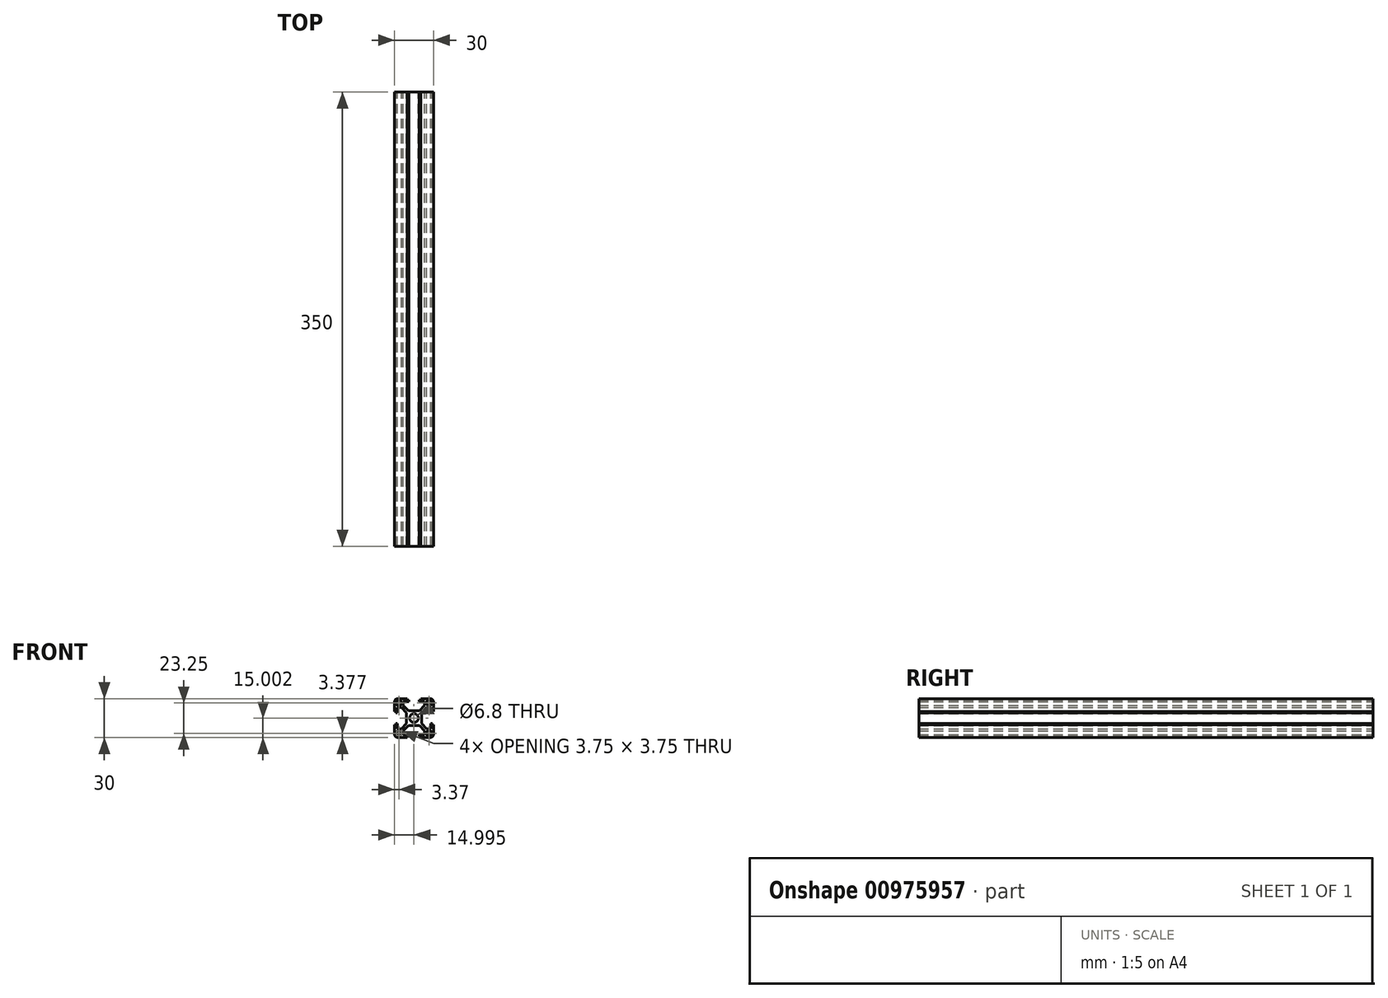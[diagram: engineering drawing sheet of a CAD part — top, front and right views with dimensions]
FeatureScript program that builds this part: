
annotation { "Feature Type Name" : "Feature", "Feature Type Description" : "" }
export const myFeature = defineFeature(function(context is Context, id is Id, definition is map)
    precondition{}
    {
        {
            var Q0;
            Q0=qCreatedBy(makeId("Front.planeOp"),FACE);
            var sketch = newSketch(context, id + "F0", { "sketchPlane" : qUnion([Q0])});
            skLineSegment(sketch, "E0.bottom", {"start": v(-60.67, 38.6) * mm, "end": v(-67.97, 38.6) * mm});
            skLineSegment(sketch, "E0.top", {"start": v(-60.67, 68.6) * mm, "end": v(-67.97, 68.6) * mm});
            skLineSegment(sketch, "E0.left", {"start": v(-58.17, 41.1) * mm, "end": v(-58.17, 48.4) * mm});
            skLineSegment(sketch, "E0.right", {"start": v(-88.17, 41.1) * mm, "end": v(-88.17, 48.4) * mm});
            skPoint(sketch, "E0.middle", {"position": v(-73.17, 53.6) * mm});
            skCircle(sketch, "E1", {"center": v(-73.17, 53.6) * mm, "radius": 3.4 * mm});
            skLineSegment(sketch, "E2.bottom", {"start": v(-68.93, 47.8) * mm, "end": v(-77.42, 47.8) * mm});
            skLineSegment(sketch, "E2.top", {"start": v(-68.93, 59.4) * mm, "end": v(-77.42, 59.4) * mm});
            skLineSegment(sketch, "E2.left", {"start": v(-67.37, 49.35) * mm, "end": v(-67.37, 57.84) * mm});
            skLineSegment(sketch, "E2.right", {"start": v(-78.97, 49.35) * mm, "end": v(-78.97, 57.84) * mm});
            skLineSegment(sketch, "E3.bottom", {"start": v(-60.67, 68.6) * mm, "end": v(-64.92, 68.6) * mm});
            skLineSegment(sketch, "E3.left", {"start": v(-58.17, 66.1) * mm, "end": v(-58.17, 61.84) * mm});
            skLineSegment(sketch, "E3.right", {"start": v(-64.92, 66.4) * mm, "end": v(-64.92, 63.4) * mm});
            skLineSegment(sketch, "E4.bottom", {"start": v(-60.67, 63.34) * mm, "end": v(-62.42, 63.34) * mm});
            skLineSegment(sketch, "E4.top", {"start": v(-60.67, 67.1) * mm, "end": v(-62.42, 67.1) * mm});
            skLineSegment(sketch, "E4.left", {"start": v(-59.67, 64.34) * mm, "end": v(-59.67, 66.1) * mm});
            skLineSegment(sketch, "E4.right", {"start": v(-63.42, 64.34) * mm, "end": v(-63.42, 66.1) * mm});
            skPoint(sketch, "E4.middle", {"position": v(-61.55, 65.22) * mm});
            skLineSegment(sketch, "E5", {"start": v(-63.37, 61.84) * mm, "end": v(-67.37, 57.84) * mm});
            skLineSegment(sketch, "E6.MirrorCS", {"start": v(-64.92, 63.4) * mm, "end": v(-68.93, 59.4) * mm});
            skLineSegment(sketch, "E7", {"start": v(-60.37, 61.84) * mm, "end": v(-60.37, 57.7) * mm});
            skPoint(sketch, "E8.visualSharp", {"position": v(-58.17, 68.6) * mm});
            skArc(sketch, "E8.filletArc", {"start": v(-58.17, 66.1) * mm, "mid": v(-58.9, 67.86) * mm, "end": v(-60.67, 68.6) * mm});
            skLineSegment(sketch, "E9.MirrorCS", {"start": v(-60.37, 45.34) * mm, "end": v(-60.37, 49.5) * mm});
            skLineSegment(sketch, "E10", {"start": v(-58.17, 61.84) * mm, "end": v(-58.17, 58.8) * mm});
            skLineSegment(sketch, "E11", {"start": v(-58.97, 58.8) * mm, "end": v(-58.17, 58.8) * mm});
            skLineSegment(sketch, "E12", {"start": v(-59.17, 58.6) * mm, "end": v(-59.17, 57.7) * mm});
            skLineSegment(sketch, "E13", {"start": v(-60.37, 57.7) * mm, "end": v(-59.17, 57.7) * mm});
            skPoint(sketch, "E14.visualSharp", {"position": v(-59.17, 58.8) * mm});
            skArc(sketch, "E14.filletArc", {"start": v(-58.97, 58.8) * mm, "mid": v(-59.12, 58.73) * mm, "end": v(-59.17, 58.6) * mm});
            skLineSegment(sketch, "E15.MirrorCS", {"start": v(-64.92, 66.4) * mm, "end": v(-69.07, 66.4) * mm});
            skLineSegment(sketch, "E16.MirrorCS", {"start": v(-69.07, 66.4) * mm, "end": v(-69.07, 67.6) * mm});
            skLineSegment(sketch, "E17.MirrorCS", {"start": v(-68.27, 67.6) * mm, "end": v(-69.07, 67.6) * mm});
            skLineSegment(sketch, "E18.MirrorCS", {"start": v(-67.97, 67.9) * mm, "end": v(-67.97, 68.6) * mm});
            skArc(sketch, "E19.MirrorCS", {"start": v(-67.97, 67.9) * mm, "mid": v(-68.06, 67.68) * mm, "end": v(-68.27, 67.6) * mm});
            skLineSegment(sketch, "E20.MirrorCS", {"start": v(-64.92, 43.79) * mm, "end": v(-68.93, 47.8) * mm});
            skLineSegment(sketch, "E21.MirrorCS", {"start": v(-63.37, 45.34) * mm, "end": v(-67.37, 49.35) * mm});
            skLineSegment(sketch, "E22.trimOffspring", {"start": v(-60.37, 61.84) * mm, "end": v(-63.37, 61.84) * mm});
            skLineSegment(sketch, "E23.MirrorCS", {"start": v(-60.37, 45.34) * mm, "end": v(-63.37, 45.34) * mm});
            skLineSegment(sketch, "E24.MirrorCS", {"start": v(-60.67, 43.84) * mm, "end": v(-62.42, 43.84) * mm});
            skLineSegment(sketch, "E25.MirrorCS", {"start": v(-63.42, 42.84) * mm, "end": v(-63.42, 41.1) * mm});
            skLineSegment(sketch, "E26.MirrorCS", {"start": v(-59.67, 42.84) * mm, "end": v(-59.67, 41.1) * mm});
            skLineSegment(sketch, "E27.MirrorCS", {"start": v(-60.67, 40.1) * mm, "end": v(-62.42, 40.1) * mm});
            skArc(sketch, "E28.MirrorCS", {"start": v(-58.17, 41.1) * mm, "mid": v(-58.9, 39.32) * mm, "end": v(-60.67, 38.6) * mm});
            skLineSegment(sketch, "E29.MirrorCS", {"start": v(-60.37, 49.5) * mm, "end": v(-59.17, 49.5) * mm});
            skLineSegment(sketch, "E30.MirrorCS", {"start": v(-59.17, 48.6) * mm, "end": v(-59.17, 49.5) * mm});
            skLineSegment(sketch, "E31.MirrorCS", {"start": v(-58.97, 48.4) * mm, "end": v(-58.17, 48.4) * mm});
            skArc(sketch, "E32.MirrorCS", {"start": v(-58.97, 48.4) * mm, "mid": v(-59.12, 48.45) * mm, "end": v(-59.17, 48.6) * mm});
            skLineSegment(sketch, "E33.MirrorCS", {"start": v(-64.92, 40.8) * mm, "end": v(-69.07, 40.8) * mm});
            skLineSegment(sketch, "E34.MirrorCS", {"start": v(-69.07, 40.8) * mm, "end": v(-69.07, 39.6) * mm});
            skArc(sketch, "E35.MirrorCS", {"start": v(-67.97, 39.3) * mm, "mid": v(-68.06, 39.5) * mm, "end": v(-68.27, 39.6) * mm});
            skLineSegment(sketch, "E36.MirrorCS", {"start": v(-67.97, 39.3) * mm, "end": v(-67.97, 38.6) * mm});
            skLineSegment(sketch, "E37.MirrorCS", {"start": v(-64.92, 40.8) * mm, "end": v(-64.92, 43.79) * mm});
            skLineSegment(sketch, "E38.MirrorCS", {"start": v(-68.27, 39.6) * mm, "end": v(-69.07, 39.6) * mm});
            skPoint(sketch, "E39.orphan", {"position": v(-58.17, 38.6) * mm});
            skLineSegment(sketch, "E40.trimOffspring", {"start": v(-58.17, 58.8) * mm, "end": v(-58.17, 66.1) * mm});
            skLineSegment(sketch, "E41.MirrorCS", {"start": v(-77.27, 66.4) * mm, "end": v(-77.27, 67.6) * mm});
            skLineSegment(sketch, "E42.MirrorCS", {"start": v(-78.07, 67.6) * mm, "end": v(-77.27, 67.6) * mm});
            skArc(sketch, "E43.MirrorCS", {"start": v(-78.37, 67.9) * mm, "mid": v(-78.29, 67.68) * mm, "end": v(-78.07, 67.6) * mm});
            skLineSegment(sketch, "E44.MirrorCS", {"start": v(-85.67, 67.1) * mm, "end": v(-83.92, 67.1) * mm});
            skLineSegment(sketch, "E45.MirrorCS", {"start": v(-81.42, 66.4) * mm, "end": v(-81.42, 63.4) * mm});
            skLineSegment(sketch, "E46.MirrorCS", {"start": v(-82.92, 64.34) * mm, "end": v(-82.92, 66.1) * mm});
            skPoint(sketch, "E47.MirrorP", {"position": v(-84.8, 65.22) * mm});
            skLineSegment(sketch, "E48.MirrorCS", {"start": v(-85.97, 61.84) * mm, "end": v(-82.98, 61.84) * mm});
            skLineSegment(sketch, "E49.MirrorCS", {"start": v(-86.67, 64.34) * mm, "end": v(-86.67, 66.1) * mm});
            skLineSegment(sketch, "E50.MirrorCS", {"start": v(-85.67, 63.34) * mm, "end": v(-83.92, 63.34) * mm});
            skLineSegment(sketch, "E51.MirrorCS", {"start": v(-81.42, 66.4) * mm, "end": v(-77.27, 66.4) * mm});
            skLineSegment(sketch, "E52.MirrorCS", {"start": v(-82.98, 61.84) * mm, "end": v(-78.97, 57.84) * mm});
            skLineSegment(sketch, "E53.MirrorCS", {"start": v(-81.42, 63.4) * mm, "end": v(-77.42, 59.4) * mm});
            skLineSegment(sketch, "E54.MirrorCS", {"start": v(-78.37, 67.9) * mm, "end": v(-78.37, 68.6) * mm});
            skLineSegment(sketch, "E55.MirrorCS", {"start": v(-87.37, 58.8) * mm, "end": v(-88.17, 58.8) * mm});
            skPoint(sketch, "E56.MirrorP", {"position": v(-87.17, 58.8) * mm});
            skArc(sketch, "E57.MirrorCS", {"start": v(-87.37, 58.8) * mm, "mid": v(-87.23, 58.73) * mm, "end": v(-87.17, 58.6) * mm});
            skLineSegment(sketch, "E58.MirrorCS", {"start": v(-87.17, 58.6) * mm, "end": v(-87.17, 57.7) * mm});
            skLineSegment(sketch, "E59.MirrorCS", {"start": v(-85.97, 61.84) * mm, "end": v(-85.97, 57.7) * mm});
            skLineSegment(sketch, "E60.MirrorCS", {"start": v(-85.97, 57.7) * mm, "end": v(-87.17, 57.7) * mm});
            skArc(sketch, "E61.MirrorCS", {"start": v(-88.17, 66.1) * mm, "mid": v(-87.44, 67.86) * mm, "end": v(-85.67, 68.6) * mm});
            skPoint(sketch, "E62.orphan", {"position": v(-88.17, 68.6) * mm});
            skLineSegment(sketch, "E63.trimOffspring", {"start": v(-78.37, 68.6) * mm, "end": v(-85.67, 68.6) * mm});
            skLineSegment(sketch, "E64.MirrorCS", {"start": v(-78.37, 39.3) * mm, "end": v(-78.37, 38.6) * mm});
            skLineSegment(sketch, "E65.MirrorCS", {"start": v(-78.07, 39.6) * mm, "end": v(-77.27, 39.6) * mm});
            skArc(sketch, "E66.MirrorCS", {"start": v(-78.37, 39.3) * mm, "mid": v(-78.29, 39.5) * mm, "end": v(-78.07, 39.6) * mm});
            skLineSegment(sketch, "E67.MirrorCS", {"start": v(-87.17, 48.6) * mm, "end": v(-87.17, 49.5) * mm});
            skLineSegment(sketch, "E68.MirrorCS", {"start": v(-77.27, 40.8) * mm, "end": v(-77.27, 39.6) * mm});
            skLineSegment(sketch, "E69.MirrorCS", {"start": v(-87.37, 48.4) * mm, "end": v(-88.17, 48.4) * mm});
            skArc(sketch, "E70.MirrorCS", {"start": v(-87.37, 48.4) * mm, "mid": v(-87.23, 48.45) * mm, "end": v(-87.17, 48.6) * mm});
            skLineSegment(sketch, "E71.MirrorCS", {"start": v(-85.97, 49.5) * mm, "end": v(-87.17, 49.5) * mm});
            skArc(sketch, "E72.MirrorCS", {"start": v(-88.17, 41.1) * mm, "mid": v(-87.44, 39.32) * mm, "end": v(-85.67, 38.6) * mm});
            skLineSegment(sketch, "E73.MirrorCS", {"start": v(-81.42, 40.8) * mm, "end": v(-81.42, 43.79) * mm});
            skLineSegment(sketch, "E74.MirrorCS", {"start": v(-81.42, 43.79) * mm, "end": v(-77.42, 47.8) * mm});
            skLineSegment(sketch, "E75.MirrorCS", {"start": v(-82.92, 42.84) * mm, "end": v(-82.92, 41.1) * mm});
            skLineSegment(sketch, "E76.MirrorCS", {"start": v(-81.42, 40.8) * mm, "end": v(-77.27, 40.8) * mm});
            skLineSegment(sketch, "E77.MirrorCS", {"start": v(-85.97, 45.34) * mm, "end": v(-85.97, 49.5) * mm});
            skLineSegment(sketch, "E78.MirrorCS", {"start": v(-85.97, 45.34) * mm, "end": v(-82.98, 45.34) * mm});
            skLineSegment(sketch, "E79.MirrorCS", {"start": v(-85.67, 43.84) * mm, "end": v(-83.92, 43.84) * mm});
            skLineSegment(sketch, "E80.MirrorCS", {"start": v(-85.67, 40.1) * mm, "end": v(-83.92, 40.1) * mm});
            skPoint(sketch, "E81.MirrorP", {"position": v(-88.17, 38.6) * mm});
            skLineSegment(sketch, "E82.MirrorCS", {"start": v(-82.98, 45.34) * mm, "end": v(-78.97, 49.35) * mm});
            skLineSegment(sketch, "E83.MirrorCS", {"start": v(-86.67, 42.84) * mm, "end": v(-86.67, 41.1) * mm});
            skLineSegment(sketch, "E84.trimOffspring", {"start": v(-78.37, 38.6) * mm, "end": v(-85.67, 38.6) * mm});
            skLineSegment(sketch, "E85.trimOffspring", {"start": v(-88.17, 58.8) * mm, "end": v(-88.17, 66.1) * mm});
            skPoint(sketch, "E86.orphan", {"position": v(-67.37, 59.4) * mm});
            skPoint(sketch, "E87.orphan", {"position": v(-78.97, 59.4) * mm});
            skPoint(sketch, "E88.orphan", {"position": v(-78.97, 47.8) * mm});
            skPoint(sketch, "E89.orphan", {"position": v(-67.37, 47.8) * mm});
            skPoint(sketch, "E90.visualSharp", {"position": v(-59.67, 67.1) * mm});
            skArc(sketch, "E90.filletArc", {"start": v(-59.67, 66.1) * mm, "mid": v(-59.97, 66.8) * mm, "end": v(-60.67, 67.1) * mm});
            skPoint(sketch, "E91.visualSharp", {"position": v(-63.42, 67.1) * mm});
            skArc(sketch, "E91.filletArc", {"start": v(-62.42, 67.1) * mm, "mid": v(-63.13, 66.8) * mm, "end": v(-63.42, 66.1) * mm});
            skPoint(sketch, "E92.visualSharp", {"position": v(-63.42, 63.34) * mm});
            skArc(sketch, "E92.filletArc", {"start": v(-63.42, 64.34) * mm, "mid": v(-63.13, 63.63) * mm, "end": v(-62.42, 63.34) * mm});
            skPoint(sketch, "E93.visualSharp", {"position": v(-59.67, 63.34) * mm});
            skArc(sketch, "E93.filletArc", {"start": v(-60.67, 63.34) * mm, "mid": v(-59.97, 63.63) * mm, "end": v(-59.67, 64.34) * mm});
            skArc(sketch, "E94.MirrorCS", {"start": v(-63.42, 42.84) * mm, "mid": v(-63.13, 43.55) * mm, "end": v(-62.42, 43.84) * mm});
            skArc(sketch, "E95.MirrorCS", {"start": v(-60.67, 43.84) * mm, "mid": v(-59.97, 43.55) * mm, "end": v(-59.67, 42.84) * mm});
            skArc(sketch, "E96.MirrorCS", {"start": v(-62.42, 40.1) * mm, "mid": v(-63.13, 40.38) * mm, "end": v(-63.42, 41.1) * mm});
            skArc(sketch, "E97.MirrorCS", {"start": v(-59.67, 41.1) * mm, "mid": v(-59.97, 40.38) * mm, "end": v(-60.67, 40.1) * mm});
            skArc(sketch, "E98.MirrorCS", {"start": v(-83.92, 67.1) * mm, "mid": v(-83.22, 66.8) * mm, "end": v(-82.92, 66.1) * mm});
            skArc(sketch, "E99.MirrorCS", {"start": v(-82.92, 64.34) * mm, "mid": v(-83.22, 63.63) * mm, "end": v(-83.92, 63.34) * mm});
            skArc(sketch, "E100.MirrorCS", {"start": v(-85.67, 63.34) * mm, "mid": v(-86.38, 63.63) * mm, "end": v(-86.67, 64.34) * mm});
            skArc(sketch, "E101.MirrorCS", {"start": v(-86.67, 66.1) * mm, "mid": v(-86.38, 66.8) * mm, "end": v(-85.67, 67.1) * mm});
            skArc(sketch, "E102.MirrorCS", {"start": v(-82.92, 42.84) * mm, "mid": v(-83.22, 43.55) * mm, "end": v(-83.92, 43.84) * mm});
            skArc(sketch, "E103.MirrorCS", {"start": v(-85.67, 43.84) * mm, "mid": v(-86.38, 43.55) * mm, "end": v(-86.67, 42.84) * mm});
            skArc(sketch, "E104.MirrorCS", {"start": v(-86.67, 41.1) * mm, "mid": v(-86.38, 40.38) * mm, "end": v(-85.67, 40.1) * mm});
            skArc(sketch, "E105.MirrorCS", {"start": v(-83.92, 40.1) * mm, "mid": v(-83.22, 40.38) * mm, "end": v(-82.92, 41.1) * mm});
            skPoint(sketch, "E106.orphan", {"position": v(-59.67, 43.84) * mm});
            skPoint(sketch, "E107.orphan", {"position": v(-63.42, 43.84) * mm});
            skPoint(sketch, "E108.orphan", {"position": v(-63.42, 40.1) * mm});
            skPoint(sketch, "E109.orphan", {"position": v(-59.67, 40.1) * mm});
            skPoint(sketch, "E110.orphan", {"position": v(-86.67, 43.84) * mm});
            skPoint(sketch, "E111.orphan", {"position": v(-82.92, 43.84) * mm});
            skPoint(sketch, "E112.orphan", {"position": v(-82.92, 40.1) * mm});
            skPoint(sketch, "E113.orphan", {"position": v(-86.67, 40.1) * mm});
            skPoint(sketch, "E114.orphan", {"position": v(-82.92, 67.1) * mm});
            skPoint(sketch, "E115.orphan", {"position": v(-86.67, 67.1) * mm});
            skPoint(sketch, "E116.orphan", {"position": v(-86.67, 63.34) * mm});
            skPoint(sketch, "E117.orphan", {"position": v(-82.92, 63.34) * mm});
            skSolve(sketch);
        }
        {
            var Q0;
            Q0=makeQuery(id+"F0.imprint","IMPRINT",FACE,{"disambiguationData":[TD([[makeQuery(id+"F0.imprint","IMPRINT",EDGE,{"derivedFrom":sQuery(id+"F0.wireOp",EDGE,"E0.bottom")}),-1.0]])]});
            extrude(context, id + "F1", {"entities" : qUnion([Q0]), "depth" : 350 * mm, "offsetDistance" : 25 * mm});
        }
    });
